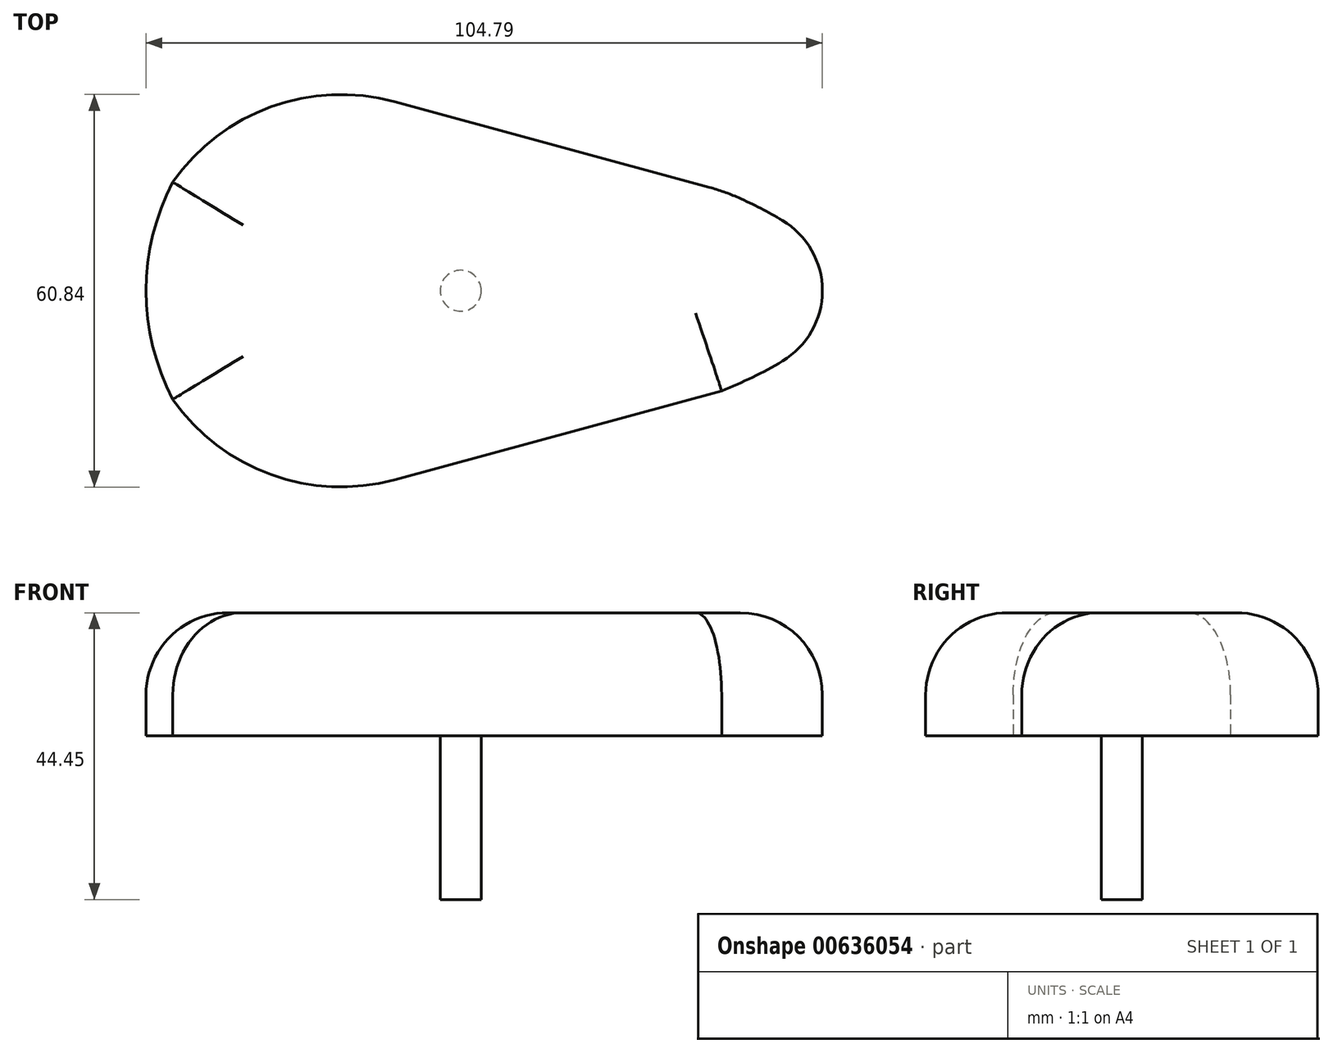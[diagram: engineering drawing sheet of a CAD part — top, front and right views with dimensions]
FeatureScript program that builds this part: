
annotation { "Feature Type Name" : "Feature", "Feature Type Description" : "" }
export const myFeature = defineFeature(function(context is Context, id is Id, definition is map)
    precondition{}
    {
        {
            var Q0;
            Q0=qCreatedBy(makeId("Top.planeOp"),FACE);
            var sketch = newSketch(context, id + "F0", { "sketchPlane" : qUnion([Q0])});
            skCircle(sketch, "E0", {"center": v(0, 0) * mm, "radius": 3.18 * mm});
            skLineSegment(sketch, "E1", {"start": v(-10.24, 29.3) * mm, "end": v(38.5, 16.04) * mm});
            skArc(sketch, "E2", {"start": v(49.83, 10.91) * mm, "mid": v(46.48, 12.77) * mm, "end": v(43.03, 14.43) * mm});
            skArc(sketch, "E3.MirrorCS", {"start": v(49.83, -10.91) * mm, "mid": v(45.22, -13.4) * mm, "end": v(40.43, -15.52) * mm});
            skLineSegment(sketch, "E4.MirrorCS", {"start": v(-10.24, -29.3) * mm, "end": v(40.43, -15.52) * mm});
            skPoint(sketch, "E5.visualSharp", {"position": v(-19.23, 31.75) * mm});
            skArc(sketch, "E5.filletArc", {"start": v(-10.24, 29.3) * mm, "mid": v(-29.4, 28.51) * mm, "end": v(-44.61, 16.83) * mm});
            skPoint(sketch, "E6.visualSharp", {"position": v(40.43, 15.52) * mm});
            skArc(sketch, "E6.filletArc", {"start": v(43.03, 14.43) * mm, "mid": v(40.8, 15.32) * mm, "end": v(38.5, 16.04) * mm});
            skPoint(sketch, "E7.visualSharp", {"position": v(-19.23, -31.75) * mm});
            skArc(sketch, "E7.filletArc", {"start": v(-44.61, -16.83) * mm, "mid": v(-29.4, -28.51) * mm, "end": v(-10.24, -29.3) * mm});
            skArc(sketch, "E8", {"start": v(-44.61, 16.83) * mm, "mid": v(-48.76, 0) * mm, "end": v(-44.61, -16.83) * mm});
            skPoint(sketch, "E9.visualSharp", {"position": v(63.5, 0) * mm});
            skArc(sketch, "E9.filletArc", {"start": v(49.83, -10.91) * mm, "mid": v(56.03, 0) * mm, "end": v(49.83, 10.91) * mm});
            skSolve(sketch);
        }
        {
            var Q0;
            Q0=makeQuery(id+"F0.imprint","IMPRINT",FACE,{"disambiguationData":[TD([[makeQuery(id+"F0.imprint","IMPRINT",EDGE,{"derivedFrom":sQuery(id+"F0.wireOp",EDGE,"E0")}),-1.0]])]});
            var Q1;
            Q1=makeQuery(id+"F0.imprint","IMPRINT",FACE,{"disambiguationData":[TD([[makeQuery(id+"F0.imprint","IMPRINT",EDGE,{"derivedFrom":sQuery(id+"F0.wireOp",EDGE,"E0")}),1.0]])]});
            extrude(context, id + "F1", {"entities" : qUnion([Q0, Q1]), "depth" : 19.05 * mm, "offsetDistance" : 25.4 * mm});
        }
        {
            var Q0;
            Q0=makeQuery(id+"F0.imprint","IMPRINT",FACE,{"disambiguationData":[TD([[makeQuery(id+"F0.imprint","IMPRINT",EDGE,{"derivedFrom":sQuery(id+"F0.wireOp",EDGE,"E0")}),1.0]])]});
            extrude(context, id + "F2", {"entities" : qUnion([Q0]), "operationType" : NewBodyOperationType.ADD, "oppositeDirection" : true, "depth" : 25.4 * mm, "offsetDistance" : 25.4 * mm});
        }
        {
            var Q0;
            Q0=makeQuery(id+"F1.opExtrude","CAP_FACE",FACE,{"disambiguationData":[OSD([sQuery(id+"F0.wireOp",EDGE,"E1"),sQuery(id+"F0.wireOp",EDGE,"E2"),sQuery(id+"F0.wireOp",EDGE,"E3.MirrorCS"),sQuery(id+"F0.wireOp",EDGE,"E4.MirrorCS"),sQuery(id+"F0.wireOp",EDGE,"E5.filletArc"),sQuery(id+"F0.wireOp",EDGE,"E6.filletArc"),sQuery(id+"F0.wireOp",EDGE,"E7.filletArc"),sQuery(id+"F0.wireOp",EDGE,"E8"),sQuery(id+"F0.wireOp",EDGE,"E9.filletArc")])],"isStart":false});
            fillet(context, id + "F3", {"entities" : qUnion([Q0]), "radius" : 12.7 * mm, "tangentPropagation" : true, "allowEdgeOverflow" : false});
        }
    });
